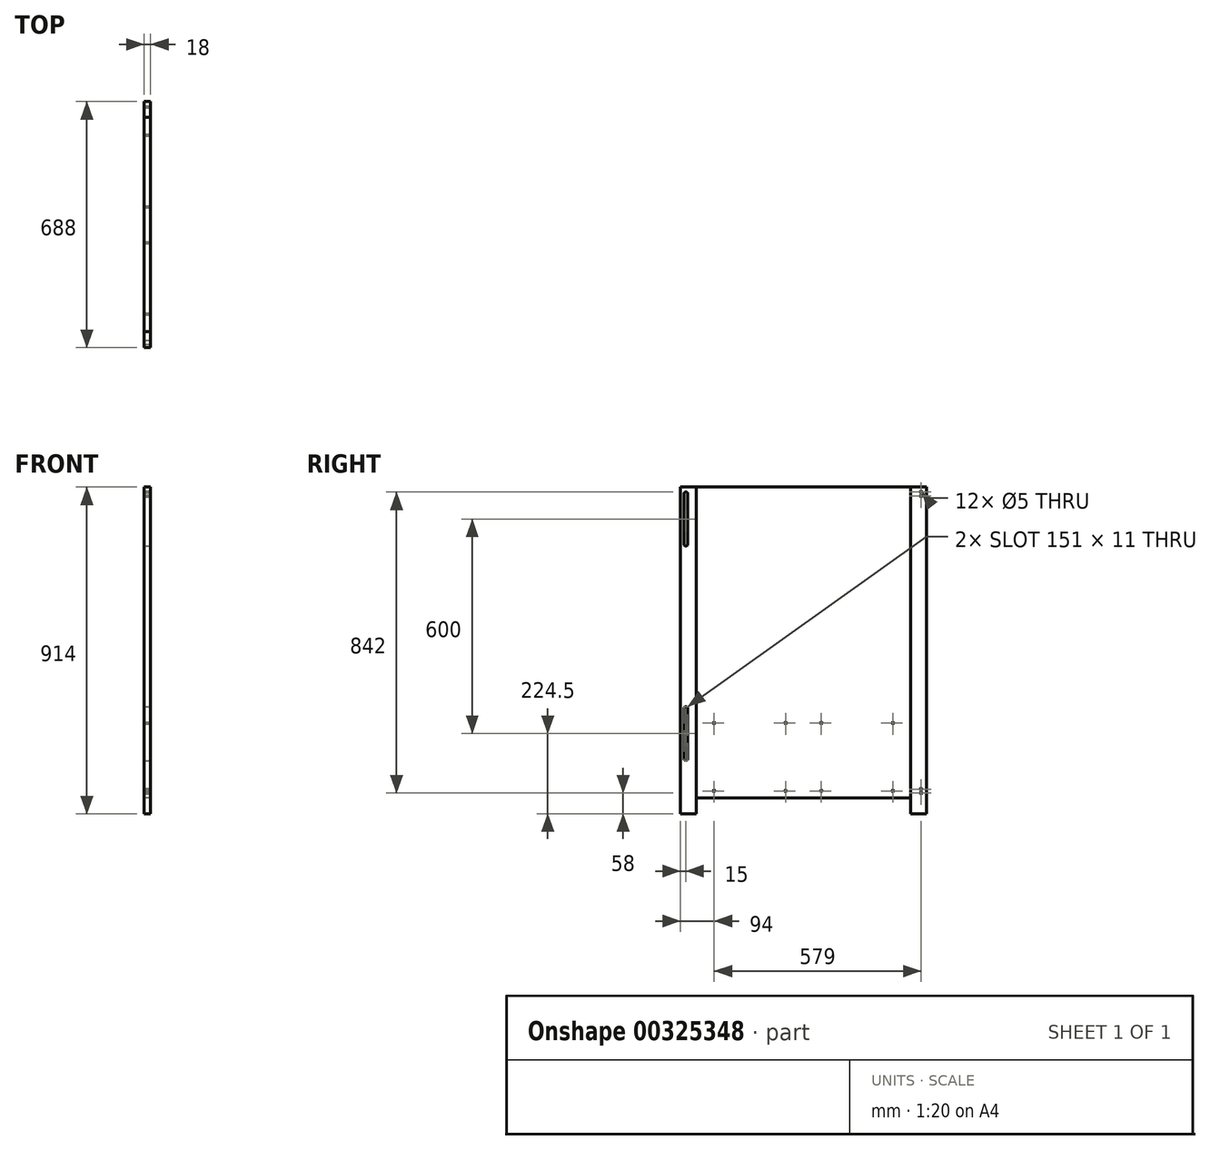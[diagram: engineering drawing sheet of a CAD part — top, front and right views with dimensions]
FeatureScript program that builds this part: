
annotation { "Feature Type Name" : "Feature", "Feature Type Description" : "" }
export const myFeature = defineFeature(function(context is Context, id is Id, definition is map)
    precondition{}
    {
        {
            var Q0;
            Q0=qCreatedBy(makeId("Right.planeOp"),FACE);
            var sketch = newSketch(context, id + "F0", { "sketchPlane" : qUnion([Q0])});
            skLineSegment(sketch, "E0.bottom", {"start": v(-300, -435) * mm, "end": v(300, -435) * mm});
            skLineSegment(sketch, "E0.top", {"start": v(-300, 435) * mm, "end": v(300, 435) * mm});
            skLineSegment(sketch, "E0.left", {"start": v(-300, -435) * mm, "end": v(-300, 435) * mm});
            skLineSegment(sketch, "E0.right", {"start": v(300, -435) * mm, "end": v(300, 435) * mm});
            skPoint(sketch, "E0.middle", {"position": v(0, 0) * mm});
            skSolve(sketch);
        }
        {
            var Q0;
            Q0 = qSketchRegion(id + "F0", true);
            extrude(context, id + "F1", {"entities" : qUnion([Q0]), "depth" : 18 * mm});
        }
        {
            var Q0;
            Q0=makeQuery(id+"F1.opExtrude","SWEPT_FACE",FACE,{"disambiguationData":[OSD([sQuery(id+"F0.wireOp",EDGE,"E0.top")])]});
            var sketch = newSketch(context, id + "F2", { "sketchPlane" : qUnion([Q0])});
            skLineSegment(sketch, "E1.bottom", {"start": v(0, -300) * mm, "end": v(18, -300) * mm});
            skLineSegment(sketch, "E1.top", {"start": v(0, -344) * mm, "end": v(18, -344) * mm});
            skLineSegment(sketch, "E1.left", {"start": v(0, -300) * mm, "end": v(0, -344) * mm});
            skLineSegment(sketch, "E1.right", {"start": v(18, -300) * mm, "end": v(18, -344) * mm});
            skLineSegment(sketch, "E2", {"start": v(18, 0) * mm, "end": v(0, 0) * mm, "construction": true});
            skLineSegment(sketch, "E3.MirrorCS", {"start": v(18, 300) * mm, "end": v(18, 344) * mm});
            skLineSegment(sketch, "E4.MirrorCS", {"start": v(0, 300) * mm, "end": v(0, 344) * mm});
            skLineSegment(sketch, "E5.MirrorCS", {"start": v(0, 300) * mm, "end": v(18, 300) * mm});
            skLineSegment(sketch, "E6.MirrorCS", {"start": v(0, 344) * mm, "end": v(18, 344) * mm});
            skSolve(sketch);
        }
        {
            var Q0;
            Q0 = qSketchRegion(id + "F2", true);
            extrude(context, id + "F3", {"entities" : qUnion([Q0]), "oppositeDirection" : true, "depth" : 914 * mm});
        }
        {
            var Q0;
            Q0=makeQuery(id+"F1.opExtrude","CAP_FACE",FACE,{"disambiguationData":[OSD([sQuery(id+"F0.wireOp",EDGE,"E0.bottom"),sQuery(id+"F0.wireOp",EDGE,"E0.top"),sQuery(id+"F0.wireOp",EDGE,"E0.left"),sQuery(id+"F0.wireOp",EDGE,"E0.right")])],"isStart":false});
            var sketch = newSketch(context, id + "F4", { "sketchPlane" : qUnion([Q0])});
            skLineSegment(sketch, "E7", {"start": v(0, -435) * mm, "end": v(0, -415) * mm, "construction": true});
            skPoint(sketch, "E7.endSnap0", {"position": v(0, -435) * mm});
            skLineSegment(sketch, "E8", {"start": v(0, -415) * mm, "end": v(250, -415) * mm, "construction": true});
            skCircle(sketch, "E9", {"center": v(250, -415) * mm, "radius": 2.5 * mm});
            skLineSegment(sketch, "E10", {"start": v(250, -415) * mm, "end": v(250, -225) * mm, "construction": true});
            skCircle(sketch, "E11", {"center": v(250, -225) * mm, "radius": 2.5 * mm});
            skCircle(sketch, "E12.1.0.0", {"center": v(50, -225) * mm, "radius": 2.5 * mm});
            skCircle(sketch, "E12.1.0.1", {"center": v(50, -415) * mm, "radius": 2.5 * mm});
            skLineSegment(sketch, "E12.direction1", {"start": v(250, -415) * mm, "end": v(50, -415) * mm, "construction": true});
            skCircle(sketch, "E13.MirrorC", {"center": v(-250, -415) * mm, "radius": 2.5 * mm});
            skCircle(sketch, "E14.MirrorC", {"center": v(-50, -225) * mm, "radius": 2.5 * mm});
            skCircle(sketch, "E15.MirrorC", {"center": v(-50, -415) * mm, "radius": 2.5 * mm});
            skCircle(sketch, "E16.MirrorC", {"center": v(-250, -225) * mm, "radius": 2.5 * mm});
            skLineSegment(sketch, "E17.bottom", {"start": v(318, 428) * mm, "end": v(340, 428) * mm, "construction": true});
            skLineSegment(sketch, "E17.top", {"start": v(318, 390) * mm, "end": v(340, 390) * mm, "construction": true});
            skLineSegment(sketch, "E17.left", {"start": v(318, 428) * mm, "end": v(318, 390) * mm, "construction": true});
            skLineSegment(sketch, "E17.right", {"start": v(340, 428) * mm, "end": v(340, 390) * mm, "construction": true});
            skLineSegment(sketch, "E18", {"start": v(329, 428) * mm, "end": v(329, 421) * mm, "construction": true});
            skLineSegment(sketch, "E19", {"start": v(329, 421) * mm, "end": v(329, 410) * mm, "construction": true});
            skCircle(sketch, "E20", {"center": v(329, 421) * mm, "radius": 2.5 * mm});
            skCircle(sketch, "E21", {"center": v(329, 410) * mm, "radius": 2.5 * mm});
            skLineSegment(sketch, "E22", {"start": v(0, 0) * mm, "end": v(-140, 0) * mm, "construction": true});
            skLineSegment(sketch, "E23.MirrorCS", {"start": v(318, -428) * mm, "end": v(340, -428) * mm, "construction": true});
            skLineSegment(sketch, "E24.MirrorCS", {"start": v(340, -428) * mm, "end": v(340, -390) * mm, "construction": true});
            skLineSegment(sketch, "E25.MirrorCS", {"start": v(318, -428) * mm, "end": v(318, -390) * mm, "construction": true});
            skLineSegment(sketch, "E26.MirrorCS", {"start": v(318, -390) * mm, "end": v(340, -390) * mm, "construction": true});
            skCircle(sketch, "E27.MirrorC", {"center": v(329, -410) * mm, "radius": 2.5 * mm});
            skCircle(sketch, "E28.MirrorC", {"center": v(329, -421) * mm, "radius": 2.5 * mm});
            skLineSegment(sketch, "E29", {"start": v(0, 0) * mm, "end": v(0, 200) * mm, "construction": true});
            skLineSegment(sketch, "E30.MirrorCS", {"start": v(-318, -428) * mm, "end": v(-318, -390) * mm, "construction": true});
            skLineSegment(sketch, "E31.MirrorCS", {"start": v(-318, -390) * mm, "end": v(-340, -390) * mm, "construction": true});
            skLineSegment(sketch, "E32.MirrorCS", {"start": v(-340, -428) * mm, "end": v(-340, -390) * mm, "construction": true});
            skLineSegment(sketch, "E33.MirrorCS", {"start": v(-318, -428) * mm, "end": v(-340, -428) * mm, "construction": true});
            skLineSegment(sketch, "E34.MirrorCS", {"start": v(-318, 390) * mm, "end": v(-340, 390) * mm, "construction": true});
            skLineSegment(sketch, "E35.MirrorCS", {"start": v(-318, 428) * mm, "end": v(-318, 390) * mm, "construction": true});
            skLineSegment(sketch, "E36.MirrorCS", {"start": v(-340, 428) * mm, "end": v(-340, 390) * mm, "construction": true});
            skLineSegment(sketch, "E37.MirrorCS", {"start": v(-318, 428) * mm, "end": v(-340, 428) * mm, "construction": true});
            skLineSegment(sketch, "E38", {"start": v(-329, 428) * mm, "end": v(-329, 415.5) * mm, "construction": true});
            skPoint(sketch, "E38.endSnap0", {"position": v(-329, 428) * mm});
            skArc(sketch, "E39", {"start": v(-323.5, 415.5) * mm, "mid": v(-329, 421) * mm, "end": v(-334.5, 415.5) * mm});
            skArc(sketch, "E40.0.1.0", {"start": v(-334.5, 275.5) * mm, "mid": v(-329, 270) * mm, "end": v(-323.5, 275.5) * mm});
            skLineSegment(sketch, "E40.direction1", {"start": v(-329, 415.5) * mm, "end": v(-304, 415.5) * mm, "construction": true});
            skLineSegment(sketch, "E40.direction2", {"start": v(-329, 415.5) * mm, "end": v(-329, 275.5) * mm, "construction": true});
            skLineSegment(sketch, "E41.0", {"start": v(-334.5, 415.5) * mm, "end": v(-334.5, 275.5) * mm});
            skLineSegment(sketch, "E42.0", {"start": v(-323.5, 415.5) * mm, "end": v(-323.5, 275.5) * mm});
            skLineSegment(sketch, "E43.0.1.0", {"start": v(-334.5, -184.5) * mm, "end": v(-334.5, -324.5) * mm});
            skArc(sketch, "E43.0.1.2", {"start": v(-323.5, -184.5) * mm, "mid": v(-329, -179) * mm, "end": v(-334.5, -184.5) * mm});
            skArc(sketch, "E43.0.1.3", {"start": v(-334.5, -324.5) * mm, "mid": v(-329, -330) * mm, "end": v(-323.5, -324.5) * mm});
            skLineSegment(sketch, "E43.direction1", {"start": v(-334.5, 275.5) * mm, "end": v(-313.5, 275.5) * mm, "construction": true});
            skLineSegment(sketch, "E43.direction2", {"start": v(-334.5, 275.5) * mm, "end": v(-334.5, -324.5) * mm, "construction": true});
            skLineSegment(sketch, "E44", {"start": v(-323.5, -324.5) * mm, "end": v(-323.5, -184.5) * mm});
            skLineSegment(sketch, "E45", {"start": v(-334.5, 345.5) * mm, "end": v(-323.5, 345.5) * mm});
            skSolve(sketch);
        }
        {
            var Q0;
            Q0 = qSketchRegion(id + "F4", true);
            extrude(context, id + "F5", {"entities" : qUnion([Q0]), "operationType" : NewBodyOperationType.REMOVE, "oppositeDirection" : true, "depth" : 18 * mm});
        }
    });
